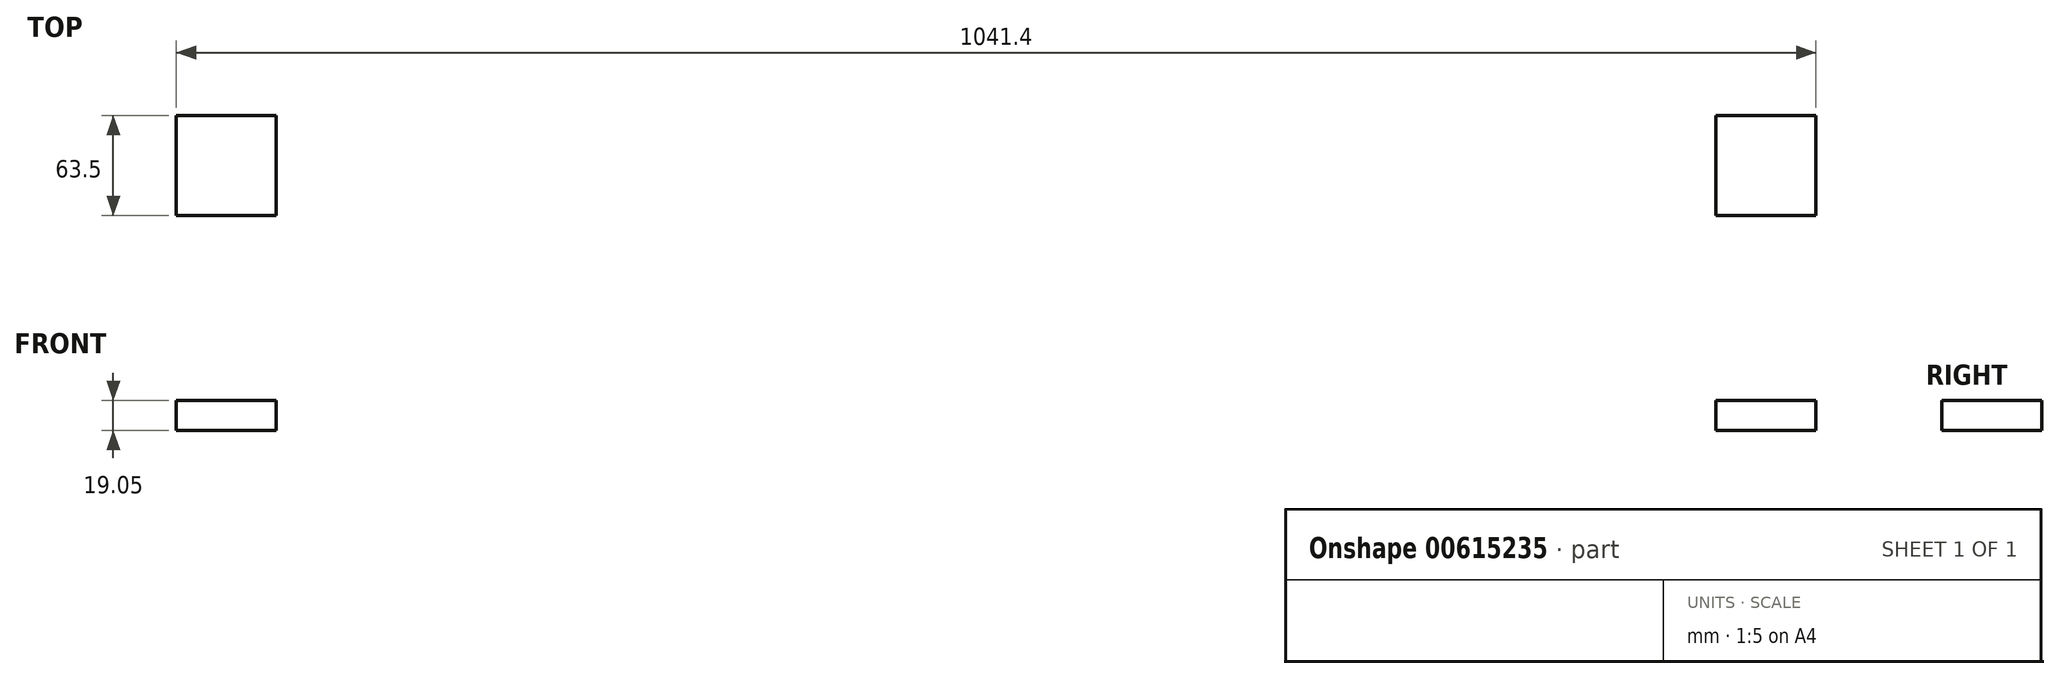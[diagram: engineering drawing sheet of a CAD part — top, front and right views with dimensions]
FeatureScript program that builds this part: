
annotation { "Feature Type Name" : "Feature", "Feature Type Description" : "" }
export const myFeature = defineFeature(function(context is Context, id is Id, definition is map)
    precondition{}
    {
        {
            var Q0;
            Q0=qCreatedBy(makeId("Top.planeOp"),FACE);
            var sketch = newSketch(context, id + "F0", { "sketchPlane" : qUnion([Q0])});
            skLineSegment(sketch, "E0.bottom", {"start": v(0, 0) * mm, "end": v(1041.4, 0) * mm});
            skLineSegment(sketch, "E0.top", {"start": v(0, 635) * mm, "end": v(1041.4, 635) * mm});
            skLineSegment(sketch, "E0.left", {"start": v(0, 0) * mm, "end": v(0, 635) * mm});
            skLineSegment(sketch, "E0.right", {"start": v(1041.4, 0) * mm, "end": v(1041.4, 635) * mm});
            skLineSegment(sketch, "E1.bottom", {"start": v(1041.4, 0) * mm, "end": v(977.9, 0) * mm});
            skLineSegment(sketch, "E1.top", {"start": v(1041.4, 63.5) * mm, "end": v(977.9, 63.5) * mm});
            skLineSegment(sketch, "E1.left", {"start": v(1041.4, 0) * mm, "end": v(1041.4, 63.5) * mm});
            skLineSegment(sketch, "E1.right", {"start": v(977.9, 0) * mm, "end": v(977.9, 63.5) * mm});
            skLineSegment(sketch, "E2.bottom", {"start": v(1041.4, 635) * mm, "end": v(977.9, 635) * mm});
            skLineSegment(sketch, "E2.top", {"start": v(1041.4, 571.5) * mm, "end": v(977.9, 571.5) * mm});
            skLineSegment(sketch, "E2.left", {"start": v(1041.4, 635) * mm, "end": v(1041.4, 571.5) * mm});
            skLineSegment(sketch, "E2.right", {"start": v(977.9, 635) * mm, "end": v(977.9, 571.5) * mm});
            skLineSegment(sketch, "E3.bottom", {"start": v(0, 0) * mm, "end": v(63.5, 0) * mm});
            skLineSegment(sketch, "E3.top", {"start": v(0, 63.5) * mm, "end": v(63.5, 63.5) * mm});
            skLineSegment(sketch, "E3.left", {"start": v(0, 0) * mm, "end": v(0, 63.5) * mm});
            skLineSegment(sketch, "E3.right", {"start": v(63.5, 0) * mm, "end": v(63.5, 63.5) * mm});
            skLineSegment(sketch, "E4.bottom", {"start": v(0, 635) * mm, "end": v(63.5, 635) * mm});
            skLineSegment(sketch, "E4.top", {"start": v(0, 571.5) * mm, "end": v(63.5, 571.5) * mm});
            skLineSegment(sketch, "E4.left", {"start": v(0, 635) * mm, "end": v(0, 571.5) * mm});
            skLineSegment(sketch, "E4.right", {"start": v(63.5, 635) * mm, "end": v(63.5, 571.5) * mm});
            skSolve(sketch);
        }
        {
            var Q0;
            Q0=makeQuery(id+"F0.imprint","IMPRINT",FACE,{"disambiguationData":[TD([[makeQuery(id+"F0.imprint","IMPRINT",EDGE,{"derivedFrom":sQuery(id+"F0.wireOp",EDGE,"E0.bottom")}),1.0]])]});
            extrude(context, id + "F1", {"entities" : qUnion([Q0]), "depth" : 19.05 * mm, "offsetDistance" : 25.4 * mm});
        }
    });
